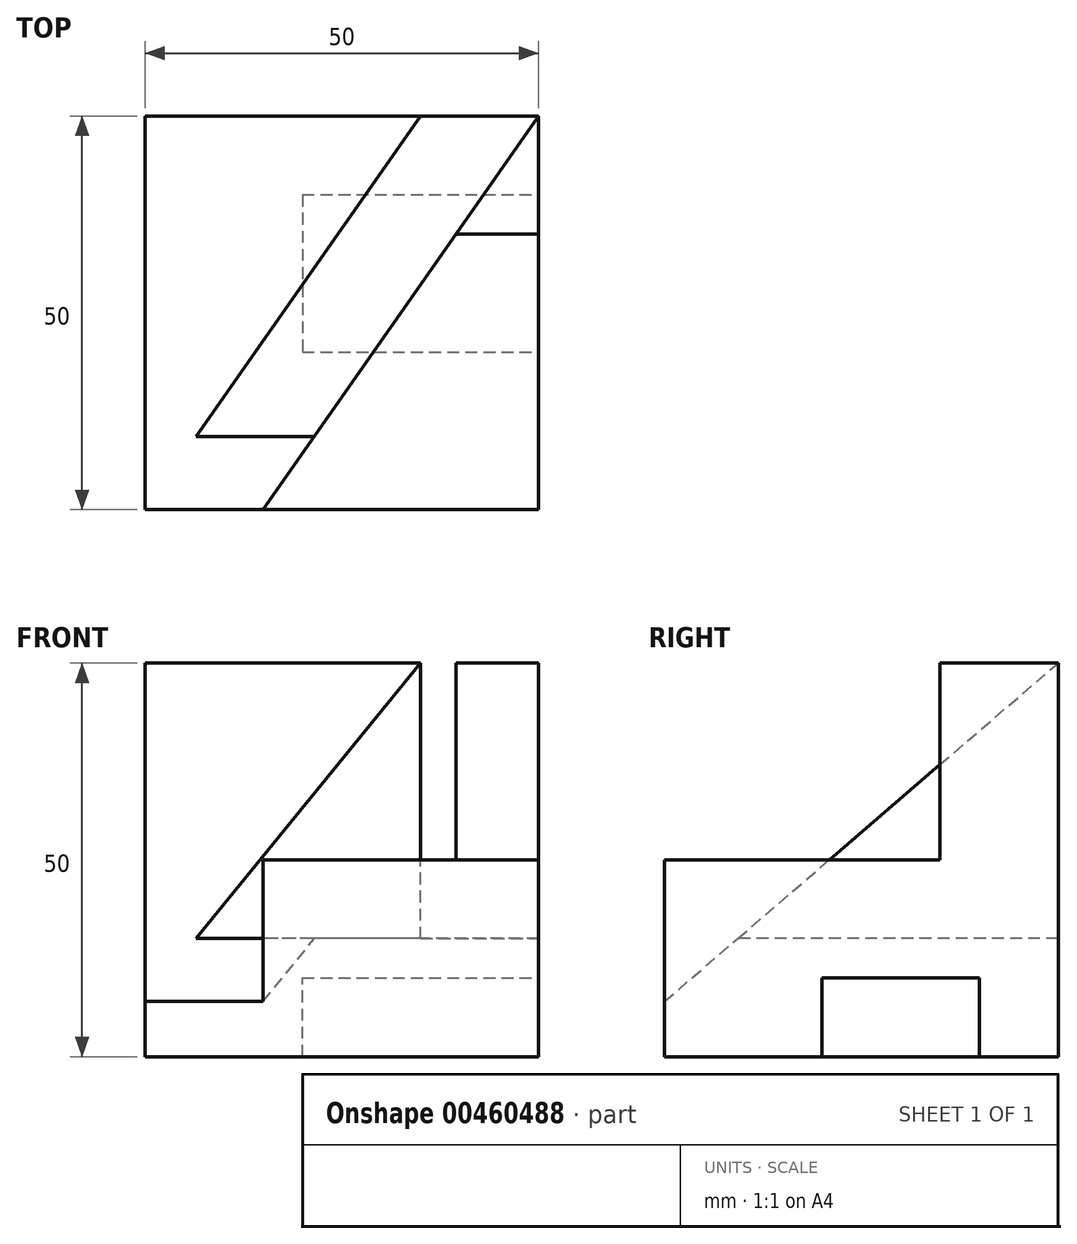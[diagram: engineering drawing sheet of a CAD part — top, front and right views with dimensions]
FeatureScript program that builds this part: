
annotation { "Feature Type Name" : "Feature", "Feature Type Description" : "" }
export const myFeature = defineFeature(function(context is Context, id is Id, definition is map)
    precondition{}
    {
        {
            var Q0;
            Q0=qCreatedBy(makeId("Top.planeOp"),FACE);
            var sketch = newSketch(context, id + "F0", { "sketchPlane" : qUnion([Q0])});
            skLineSegment(sketch, "E0.bottom", {"start": v(0, 0) * mm, "end": v(50, 0) * mm});
            skLineSegment(sketch, "E0.top", {"start": v(0, -50) * mm, "end": v(50, -50) * mm});
            skLineSegment(sketch, "E0.left", {"start": v(0, 0) * mm, "end": v(0, -50) * mm});
            skLineSegment(sketch, "E0.right", {"start": v(50, 0) * mm, "end": v(50, -50) * mm});
            skSolve(sketch);
        }
        {
            var Q0;
            Q0 = qSketchRegion(id + "F0", true);
            extrude(context, id + "F1", {"entities" : qUnion([Q0]), "depth" : 50 * mm});
        }
        {
            var Q0;
            Q0=makeQuery(id+"F1.opExtrude","CAP_FACE",FACE,{"disambiguationData":[OSD([sQuery(id+"F0.wireOp",EDGE,"E0.bottom"),sQuery(id+"F0.wireOp",EDGE,"E0.top"),sQuery(id+"F0.wireOp",EDGE,"E0.left"),sQuery(id+"F0.wireOp",EDGE,"E0.right")])],"isStart":false});
            var sketch = newSketch(context, id + "F2", { "sketchPlane" : qUnion([Q0])});
            skLineSegment(sketch, "E1", {"start": v(50, 0) * mm, "end": v(15, -50) * mm});
            skLineSegment(sketch, "E2", {"start": v(15, -50) * mm, "end": v(50, -50) * mm});
            skLineSegment(sketch, "E3", {"start": v(50, 0) * mm, "end": v(50, -50) * mm});
            skSolve(sketch);
        }
        {
            var Q0;
            Q0=makeQuery(id+"F2.imprint","IMPRINT",FACE,{"disambiguationData":[TD([[makeQuery(id+"F2.imprint","IMPRINT",EDGE,{"derivedFrom":sQuery(id+"F2.wireOp",EDGE,"E1")}),1.0]])]});
            var Q1;
            Q1=makeQuery(id+"F1.opExtrude","SWEPT_FACE",FACE,{"disambiguationData":[OSD([sQuery(id+"F0.wireOp",EDGE,"E0.top")])]});
            extrude(context, id + "F3", {"entities" : qUnion([Q0]), "operationType" : NewBodyOperationType.REMOVE, "oppositeDirection" : true, "endBoundEntityFace" : qUnion([Q1]), "depth" : 25 * mm});
        }
        {
            var Q0;
            Q0=makeQuery(id+"F1.opExtrude","CAP_FACE",FACE,{"disambiguationData":[OSD([sQuery(id+"F0.wireOp",EDGE,"E0.bottom"),sQuery(id+"F0.wireOp",EDGE,"E0.top"),sQuery(id+"F0.wireOp",EDGE,"E0.left"),sQuery(id+"F0.wireOp",EDGE,"E0.right")])],"isStart":false});
            var sketch = newSketch(context, id + "F4", { "sketchPlane" : qUnion([Q0])});
            skLineSegment(sketch, "E4", {"start": v(50, 0) * mm, "end": v(35, 0) * mm});
            skLineSegment(sketch, "E5", {"start": v(35, 0) * mm, "end": v(0, -50) * mm});
            skLineSegment(sketch, "E6", {"start": v(0, -50) * mm, "end": v(15, -50) * mm});
            skLineSegment(sketch, "E7", {"start": v(15, -50) * mm, "end": v(50, 0) * mm});
            skSolve(sketch);
        }
        {
            var Q0;
            Q0=makeQuery(id+"F1.opExtrude","CAP_FACE",FACE,{"disambiguationData":[OSD([sQuery(id+"F0.wireOp",EDGE,"E0.bottom"),sQuery(id+"F0.wireOp",EDGE,"E0.top"),sQuery(id+"F0.wireOp",EDGE,"E0.left"),sQuery(id+"F0.wireOp",EDGE,"E0.right")])],"isStart":true});
            cPlane(context, id + "F5", {"entities" : qUnion([Q0]), "cplaneType" : CPlaneType.OFFSET, "offset" : 15 * mm, "oppositeDirection" : true, "width" : 150 * mm, "height" : 150 * mm});
        }
        {
            var Q0;
            Q0=makeQuery(id+"FcdeA3PZiUrfcDw_1.splitOp","SPLIT",FACE,{"derivedFrom":makeQuery(id+"F3.boolean.opBoolean","COPY",FACE,{"derivedFrom":makeQuery(id+"F3.opExtrude","CAP_FACE",FACE,{"disambiguationData":[OSD([sQuery(id+"F2.wireOp",EDGE,"E1"),sQuery(id+"F2.wireOp",EDGE,"E2"),sQuery(id+"F2.wireOp",EDGE,"E3")])],"isStart":false})}),"isFromBackBody":true});
            extrude(context, id + "F6", {"entities" : qUnion([Q0]), "operationType" : NewBodyOperationType.ADD, "depth" : 25 * mm});
        }
        {
            var Q0;
            Q0=makeQuery(id+"F6.opExtrude","CAP_FACE",FACE,{"disambiguationData":[OSD([sQuery(id+"F2.wireOp",EDGE,"E1"),sQuery(id+"F2.wireOp",EDGE,"E2"),sQuery(id+"F2.wireOp",EDGE,"E3")])],"isStart":false});
            var sketch = newSketch(context, id + "F7", { "sketchPlane" : qUnion([Q0])});
            skLineSegment(sketch, "E8", {"start": v(50, -50) * mm, "end": v(50, -15) * mm});
            skLineSegment(sketch, "E9", {"start": v(50, -15) * mm, "end": v(39.5, -15) * mm});
            skLineSegment(sketch, "E10", {"start": v(39.5, -15) * mm, "end": v(15, -50) * mm});
            skLineSegment(sketch, "E11", {"start": v(15, -50) * mm, "end": v(50, -50) * mm});
            skSolve(sketch);
        }
        {
            var Q0;
            Q0 = qSketchRegion(id + "F7", true);
            extrude(context, id + "F8", {"entities" : qUnion([Q0]), "operationType" : NewBodyOperationType.REMOVE, "oppositeDirection" : true, "depth" : 25 * mm});
        }
        {
            var Q0;
            Q0=makeQuery(id+"FArAp3u41Hvfjml_1.splitOp","SPLIT",FACE,{"derivedFrom":makeQuery(id+"F6.boolean.opBoolean","MERGE",FACE,{"derivedFrom":[makeQuery(id+"F1.opExtrude","SWEPT_FACE",FACE,{"disambiguationData":[OSD([sQuery(id+"F0.wireOp",EDGE,"E0.right")])]}),makeQuery(id+"F6.opExtrude","SWEPT_FACE",FACE,{"disambiguationData":[OSD([sQuery(id+"F2.wireOp",EDGE,"E3")])]})]}),"isFromBackBody":true});
            var sketch = newSketch(context, id + "F9", { "sketchPlane" : qUnion([Q0])});
            skLineSegment(sketch, "E12.bottom", {"start": v(-30, 0) * mm, "end": v(-10, 0) * mm});
            skLineSegment(sketch, "E12.top", {"start": v(-30, 10) * mm, "end": v(-10, 10) * mm});
            skLineSegment(sketch, "E12.left", {"start": v(-30, 0) * mm, "end": v(-30, 10) * mm});
            skLineSegment(sketch, "E12.right", {"start": v(-10, 0) * mm, "end": v(-10, 10) * mm});
            skSolve(sketch);
        }
        {
            var Q0;
            Q0=makeQuery(id+"FArAp3u41Hvfjml_1.splitOp","SPLIT",FACE,{"derivedFrom":makeQuery(id+"F1.opExtrude","SWEPT_FACE",FACE,{"disambiguationData":[OSD([sQuery(id+"F0.wireOp",EDGE,"E0.left")])]}),"isFromBackBody":true});
            cPlane(context, id + "F10", {"entities" : qUnion([Q0]), "cplaneType" : CPlaneType.OFFSET, "offset" : 20 * mm, "oppositeDirection" : true, "width" : 150 * mm, "height" : 150 * mm});
        }
        {
            var Q0;
            Q0=makeQuery(id+"F9.imprint","IMPRINT",FACE,{"disambiguationData":[TD([[makeQuery(id+"F9.imprint","IMPRINT",EDGE,{"derivedFrom":sQuery(id+"F9.wireOp",EDGE,"E12.bottom")}),-1.0]])]});
            var Q1;
            Q1=qCreatedBy(id+"F10.planeOp",FACE);
            extrude(context, id + "F11", {"entities" : qUnion([Q0]), "operationType" : NewBodyOperationType.REMOVE, "endBound" : BoundingType.UP_TO_SURFACE, "oppositeDirection" : true, "endBoundEntityFace" : qUnion([Q1]), "depth" : 25 * mm});
        }
        {
            var Q0;
            Q0=makeQuery(id+"F1.opExtrude","SWEPT_FACE",FACE,{"disambiguationData":[OSD([sQuery(id+"F0.wireOp",EDGE,"E0.left")])]});
            var sketch = newSketch(context, id + "F12", { "sketchPlane" : qUnion([Q0])});
            skLineSegment(sketch, "E13", {"start": v(0, 50) * mm, "end": v(50, 7) * mm});
            skLineSegment(sketch, "E14", {"start": v(50, 7) * mm, "end": v(50, 50) * mm});
            skLineSegment(sketch, "E15", {"start": v(50, 50) * mm, "end": v(0, 50) * mm});
            skSolve(sketch);
        }
        {
            var Q0;
            Q0 = qSketchRegion(id + "F12", true);
            var Q1;
            Q1=makeQuery(id+"F8.boolean.opBoolean","COPY",FACE,{"derivedFrom":makeQuery(id+"F8.opExtrude","SWEPT_FACE",FACE,{"disambiguationData":[OSD([sQuery(id+"F7.wireOp",EDGE,"E10")])]})});
            extrude(context, id + "F13", {"entities" : qUnion([Q0]), "operationType" : NewBodyOperationType.REMOVE, "endBound" : BoundingType.UP_TO_SURFACE, "oppositeDirection" : true, "endBoundEntityFace" : qUnion([Q1]), "depth" : 25 * mm});
        }
        {
            var Q0;
            Q0 = qSketchRegion(id + "F4", true);
            var Q1;
            Q1=qCreatedBy(id+"F5.planeOp",FACE);
            extrude(context, id + "F14", {"entities" : qUnion([Q0]), "operationType" : NewBodyOperationType.REMOVE, "endBound" : BoundingType.UP_TO_SURFACE, "oppositeDirection" : true, "endBoundEntityFace" : qUnion([Q1]), "depth" : 25 * mm});
        }
    });
